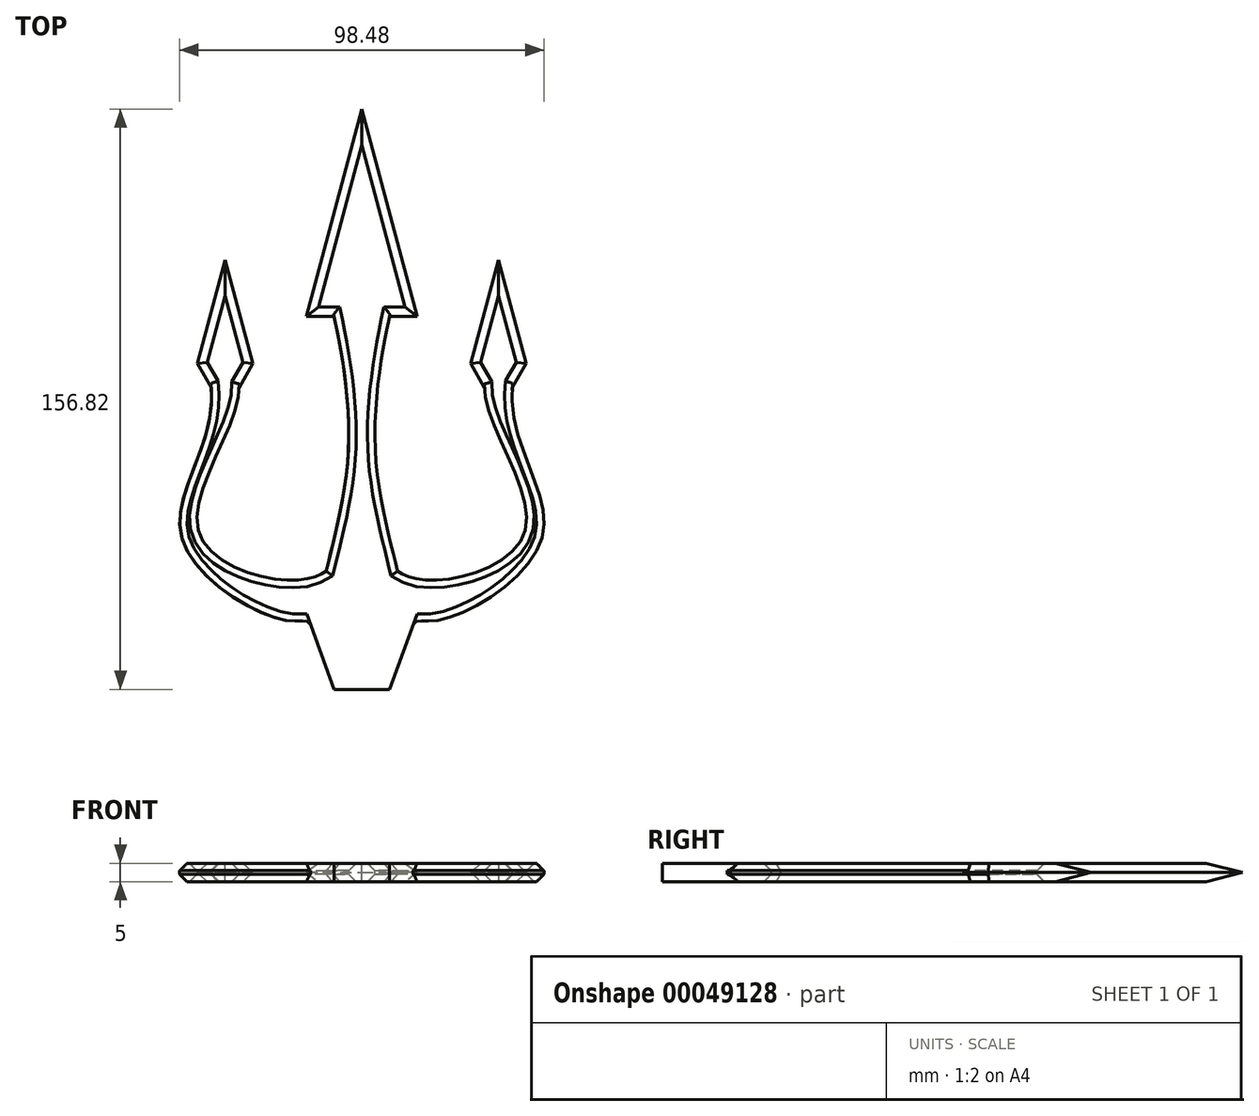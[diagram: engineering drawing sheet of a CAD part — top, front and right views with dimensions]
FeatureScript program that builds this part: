
annotation { "Feature Type Name" : "Feature", "Feature Type Description" : "" }
export const myFeature = defineFeature(function(context is Context, id is Id, definition is map)
    precondition{}
    {
        {
            var Q0;
            Q0=qCreatedBy(makeId("Top.planeOp"),FACE);
            var sketch = newSketch(context, id + "F0", { "sketchPlane" : qUnion([Q0])});
            skLineSegment(sketch, "E0", {"start": v(0, 55.98) * mm, "end": v(-15, 0) * mm});
            skLineSegment(sketch, "E1", {"start": v(-15, 0) * mm, "end": v(-7.5, 0) * mm});
            skPoint(sketch, "E1.endSnap0", {"position": v(-7.5, 28) * mm});
            skFitSpline(sketch, "E2", {"points": [v(-7.5, 0) * mm, v(-3.57, -34.75) * mm, v(-9.64, -68.92) * mm], "startDerivative": vector(9.36, -42.5) * mm, "endDerivative": vector(-12.29, -52.3) * mm});
            skFitSpline(sketch, "E3", {"points": [v(-9.64, -68.92) * mm, v(-20.4, -71.34) * mm, v(-44.29, -57.55) * mm, v(-33.17, -19.3) * mm], "startDerivative": vector(-25, -17.88) * mm, "endDerivative": vector(0.36, 75.46) * mm});
            skLineSegment(sketch, "E4", {"start": v(-36.92, 15.18) * mm, "end": v(-29.42, -12.8) * mm});
            skLineSegment(sketch, "E5", {"start": v(-36.92, 15.18) * mm, "end": v(-44.42, -12.8) * mm});
            skLineSegment(sketch, "E6", {"start": v(-40.67, -19.3) * mm, "end": v(-33.17, -19.3) * mm, "construction": true});
            skFitSpline(sketch, "E7", {"points": [v(-40.67, -19.3) * mm, v(-48.7, -59.91) * mm, v(-20.1, -82.26) * mm, v(-13.87, -83.34) * mm], "startDerivative": vector(9.41, -109.56) * mm, "endDerivative": vector(12.55, -29.13) * mm});
            skLineSegment(sketch, "E8", {"start": v(-13.87, -83.34) * mm, "end": v(-7.5, -100.84) * mm});
            skLineSegment(sketch, "E9", {"start": v(-7.5, -100.84) * mm, "end": v(0, -100.84) * mm});
            skLineSegment(sketch, "E10.MirrorCS", {"start": v(40.67, -19.3) * mm, "end": v(33.17, -19.3) * mm});
            skLineSegment(sketch, "E11.MirrorCS", {"start": v(44.42, -12.8) * mm, "end": v(40.67, -19.3) * mm});
            skLineSegment(sketch, "E12.MirrorCS", {"start": v(29.42, -12.8) * mm, "end": v(33.17, -19.3) * mm});
            skLineSegment(sketch, "E13.MirrorCS", {"start": v(0, 55.98) * mm, "end": v(15, 0) * mm});
            skLineSegment(sketch, "E14.MirrorCS", {"start": v(15, 0) * mm, "end": v(7.5, 0) * mm});
            skFitSpline(sketch, "E15.MirrorCS", {"points": [v(9.64, -68.92) * mm, v(20.4, -71.34) * mm, v(44.29, -57.55) * mm, v(33.17, -19.3) * mm], "startDerivative": vector(25, -17.88) * mm, "endDerivative": vector(-0.36, 75.46) * mm});
            skLineSegment(sketch, "E16.MirrorCS", {"start": v(36.92, 15.18) * mm, "end": v(29.42, -12.8) * mm});
            skPoint(sketch, "E17.MirrorP", {"position": v(7.5, 28) * mm});
            skLineSegment(sketch, "E18.MirrorCS", {"start": v(36.92, 15.18) * mm, "end": v(44.42, -12.8) * mm});
            skFitSpline(sketch, "E19.MirrorCS", {"points": [v(7.5, 0) * mm, v(3.57, -34.75) * mm, v(9.64, -68.92) * mm], "startDerivative": vector(-9.36, -42.5) * mm, "endDerivative": vector(12.29, -52.3) * mm});
            skFitSpline(sketch, "E20.MirrorCS", {"points": [v(40.67, -19.3) * mm, v(48.7, -59.91) * mm, v(20.1, -82.26) * mm, v(13.87, -83.34) * mm], "startDerivative": vector(-9.41, -109.56) * mm, "endDerivative": vector(-12.55, -29.13) * mm});
            skLineSegment(sketch, "E21.MirrorCS", {"start": v(7.5, -100.84) * mm, "end": v(0, -100.84) * mm});
            skLineSegment(sketch, "E22.MirrorCS", {"start": v(13.87, -83.34) * mm, "end": v(7.5, -100.84) * mm});
            skLineSegment(sketch, "E23", {"start": v(-29.42, -12.8) * mm, "end": v(-33.17, -19.3) * mm});
            skLineSegment(sketch, "E24", {"start": v(-40.67, -19.3) * mm, "end": v(-44.42, -12.8) * mm});
            skSolve(sketch);
        }
        {
            var Q0;
            Q0 = qSketchRegion(id + "F0", true);
            extrude(context, id + "F1", {"entities" : qUnion([Q0]), "depth" : 2.5 * mm, "hasSecondDirection" : true, "secondDirectionOppositeDirection" : true, "secondDirectionDepth" : 2.5 * mm});
        }
        {
            var Q0;
            Q0=makeQuery(id+"F1.opExtrude","CAP_EDGE",EDGE,{"disambiguationData":[OSD([sQuery(id+"F0.wireOp",EDGE,"E0")])],"isStart":true});
            var Q1;
            Q1=makeQuery(id+"F1.opExtrude","CAP_EDGE",EDGE,{"disambiguationData":[OSD([sQuery(id+"F0.wireOp",EDGE,"E13.MirrorCS")])],"isStart":true});
            var Q2;
            Q2=makeQuery(id+"F1.opExtrude","CAP_EDGE",EDGE,{"disambiguationData":[OSD([sQuery(id+"F0.wireOp",EDGE,"E13.MirrorCS")])],"isStart":false});
            var Q3;
            Q3=makeQuery(id+"F1.opExtrude","CAP_EDGE",EDGE,{"disambiguationData":[OSD([sQuery(id+"F0.wireOp",EDGE,"E0")])],"isStart":false});
            var Q4;
            Q4=makeQuery(id+"F1.opExtrude","CAP_EDGE",EDGE,{"disambiguationData":[OSD([sQuery(id+"F0.wireOp",EDGE,"E1")])],"isStart":false});
            var Q5;
            Q5=makeQuery(id+"F1.opExtrude","CAP_EDGE",EDGE,{"disambiguationData":[OSD([sQuery(id+"F0.wireOp",EDGE,"E1")])],"isStart":true});
            var Q6;
            Q6=makeQuery(id+"F1.opExtrude","CAP_EDGE",EDGE,{"disambiguationData":[OSD([sQuery(id+"F0.wireOp",EDGE,"E14.MirrorCS")])],"isStart":false});
            var Q7;
            Q7=makeQuery(id+"F1.opExtrude","CAP_EDGE",EDGE,{"disambiguationData":[OSD([sQuery(id+"F0.wireOp",EDGE,"E14.MirrorCS")])],"isStart":true});
            var Q8;
            Q8=makeQuery(id+"F1.opExtrude","CAP_EDGE",EDGE,{"disambiguationData":[OSD([sQuery(id+"F0.wireOp",EDGE,"E5")])],"isStart":false});
            var Q9;
            Q9=makeQuery(id+"F1.opExtrude","CAP_EDGE",EDGE,{"disambiguationData":[OSD([sQuery(id+"F0.wireOp",EDGE,"E4")])],"isStart":false});
            var Q10;
            Q10=makeQuery(id+"F1.opExtrude","CAP_EDGE",EDGE,{"disambiguationData":[OSD([sQuery(id+"F0.wireOp",EDGE,"E5")])],"isStart":true});
            var Q11;
            Q11=makeQuery(id+"F1.opExtrude","CAP_EDGE",EDGE,{"disambiguationData":[OSD([sQuery(id+"F0.wireOp",EDGE,"E4")])],"isStart":true});
            var Q12;
            Q12=makeQuery(id+"F1.opExtrude","CAP_EDGE",EDGE,{"disambiguationData":[OSD([sQuery(id+"F0.wireOp",EDGE,"E16.MirrorCS")])],"isStart":true});
            var Q13;
            Q13=makeQuery(id+"F1.opExtrude","CAP_EDGE",EDGE,{"disambiguationData":[OSD([sQuery(id+"F0.wireOp",EDGE,"E18.MirrorCS")])],"isStart":true});
            var Q14;
            Q14=makeQuery(id+"F1.opExtrude","CAP_EDGE",EDGE,{"disambiguationData":[OSD([sQuery(id+"F0.wireOp",EDGE,"E18.MirrorCS")])],"isStart":false});
            var Q15;
            Q15=makeQuery(id+"F1.opExtrude","CAP_EDGE",EDGE,{"disambiguationData":[OSD([sQuery(id+"F0.wireOp",EDGE,"E16.MirrorCS")])],"isStart":false});
            var Q16;
            Q16=makeQuery(id+"F1.opExtrude","CAP_EDGE",EDGE,{"disambiguationData":[OSD([sQuery(id+"F0.wireOp",EDGE,"E23")])],"isStart":false});
            var Q17;
            Q17=makeQuery(id+"F1.opExtrude","CAP_EDGE",EDGE,{"disambiguationData":[OSD([sQuery(id+"F0.wireOp",EDGE,"E23")])],"isStart":true});
            var Q18;
            Q18=makeQuery(id+"F1.opExtrude","CAP_EDGE",EDGE,{"disambiguationData":[OSD([sQuery(id+"F0.wireOp",EDGE,"E24")])],"isStart":false});
            var Q19;
            Q19=makeQuery(id+"F1.opExtrude","CAP_EDGE",EDGE,{"disambiguationData":[OSD([sQuery(id+"F0.wireOp",EDGE,"E24")])],"isStart":true});
            var Q20;
            Q20=makeQuery(id+"F1.opExtrude","CAP_EDGE",EDGE,{"disambiguationData":[OSD([sQuery(id+"F0.wireOp",EDGE,"E12.MirrorCS")])],"isStart":false});
            var Q21;
            Q21=makeQuery(id+"F1.opExtrude","CAP_EDGE",EDGE,{"disambiguationData":[OSD([sQuery(id+"F0.wireOp",EDGE,"E12.MirrorCS")])],"isStart":true});
            var Q22;
            Q22=makeQuery(id+"F1.opExtrude","CAP_EDGE",EDGE,{"disambiguationData":[OSD([sQuery(id+"F0.wireOp",EDGE,"E11.MirrorCS")])],"isStart":true});
            var Q23;
            Q23=makeQuery(id+"F1.opExtrude","CAP_EDGE",EDGE,{"disambiguationData":[OSD([sQuery(id+"F0.wireOp",EDGE,"E11.MirrorCS")])],"isStart":false});
            chamfer(context, id + "F2", {"entities" : qUnion([Q0, Q1, Q2, Q3, Q4, Q5, Q6, Q7, Q8, Q9, Q10, Q11, Q12, Q13, Q14, Q15, Q16, Q17, Q18, Q19, Q20, Q21, Q22, Q23]), "width" : 2.5 * mm, "tangentPropagation" : true});
        }
        {
            var Q0;
            Q0=makeQuery(id+"F1.opExtrude","CAP_EDGE",EDGE,{"disambiguationData":[OSD([sQuery(id+"F0.wireOp",EDGE,"E3")])],"isStart":false});
            var Q1;
            Q1=makeQuery(id+"F1.opExtrude","CAP_EDGE",EDGE,{"disambiguationData":[OSD([sQuery(id+"F0.wireOp",EDGE,"E7")])],"isStart":false});
            var Q2;
            Q2=makeQuery(id+"F1.opExtrude","CAP_EDGE",EDGE,{"disambiguationData":[OSD([sQuery(id+"F0.wireOp",EDGE,"E15.MirrorCS")])],"isStart":false});
            var Q3;
            Q3=makeQuery(id+"F1.opExtrude","CAP_EDGE",EDGE,{"disambiguationData":[OSD([sQuery(id+"F0.wireOp",EDGE,"E20.MirrorCS")])],"isStart":false});
            var Q4;
            Q4=makeQuery(id+"F1.opExtrude","CAP_EDGE",EDGE,{"disambiguationData":[OSD([sQuery(id+"F0.wireOp",EDGE,"E19.MirrorCS")])],"isStart":false});
            var Q5;
            Q5=makeQuery(id+"F1.opExtrude","CAP_EDGE",EDGE,{"disambiguationData":[OSD([sQuery(id+"F0.wireOp",EDGE,"E2")])],"isStart":false});
            var Q6;
            Q6=makeQuery(id+"F1.opExtrude","CAP_EDGE",EDGE,{"disambiguationData":[OSD([sQuery(id+"F0.wireOp",EDGE,"E7")])],"isStart":true});
            var Q7;
            Q7=makeQuery(id+"F1.opExtrude","CAP_EDGE",EDGE,{"disambiguationData":[OSD([sQuery(id+"F0.wireOp",EDGE,"E3")])],"isStart":true});
            var Q8;
            Q8=makeQuery(id+"F1.opExtrude","CAP_EDGE",EDGE,{"disambiguationData":[OSD([sQuery(id+"F0.wireOp",EDGE,"E2")])],"isStart":true});
            var Q9;
            Q9=makeQuery(id+"F1.opExtrude","CAP_EDGE",EDGE,{"disambiguationData":[OSD([sQuery(id+"F0.wireOp",EDGE,"E19.MirrorCS")])],"isStart":true});
            var Q10;
            Q10=makeQuery(id+"F1.opExtrude","CAP_EDGE",EDGE,{"disambiguationData":[OSD([sQuery(id+"F0.wireOp",EDGE,"E15.MirrorCS")])],"isStart":true});
            var Q11;
            Q11=makeQuery(id+"F1.opExtrude","CAP_EDGE",EDGE,{"disambiguationData":[OSD([sQuery(id+"F0.wireOp",EDGE,"E20.MirrorCS")])],"isStart":true});
            chamfer(context, id + "F3", {"entities" : qUnion([Q0, Q1, Q2, Q3, Q4, Q5, Q6, Q7, Q8, Q9, Q10, Q11]), "width" : 2 * mm, "tangentPropagation" : true});
        }
    });
